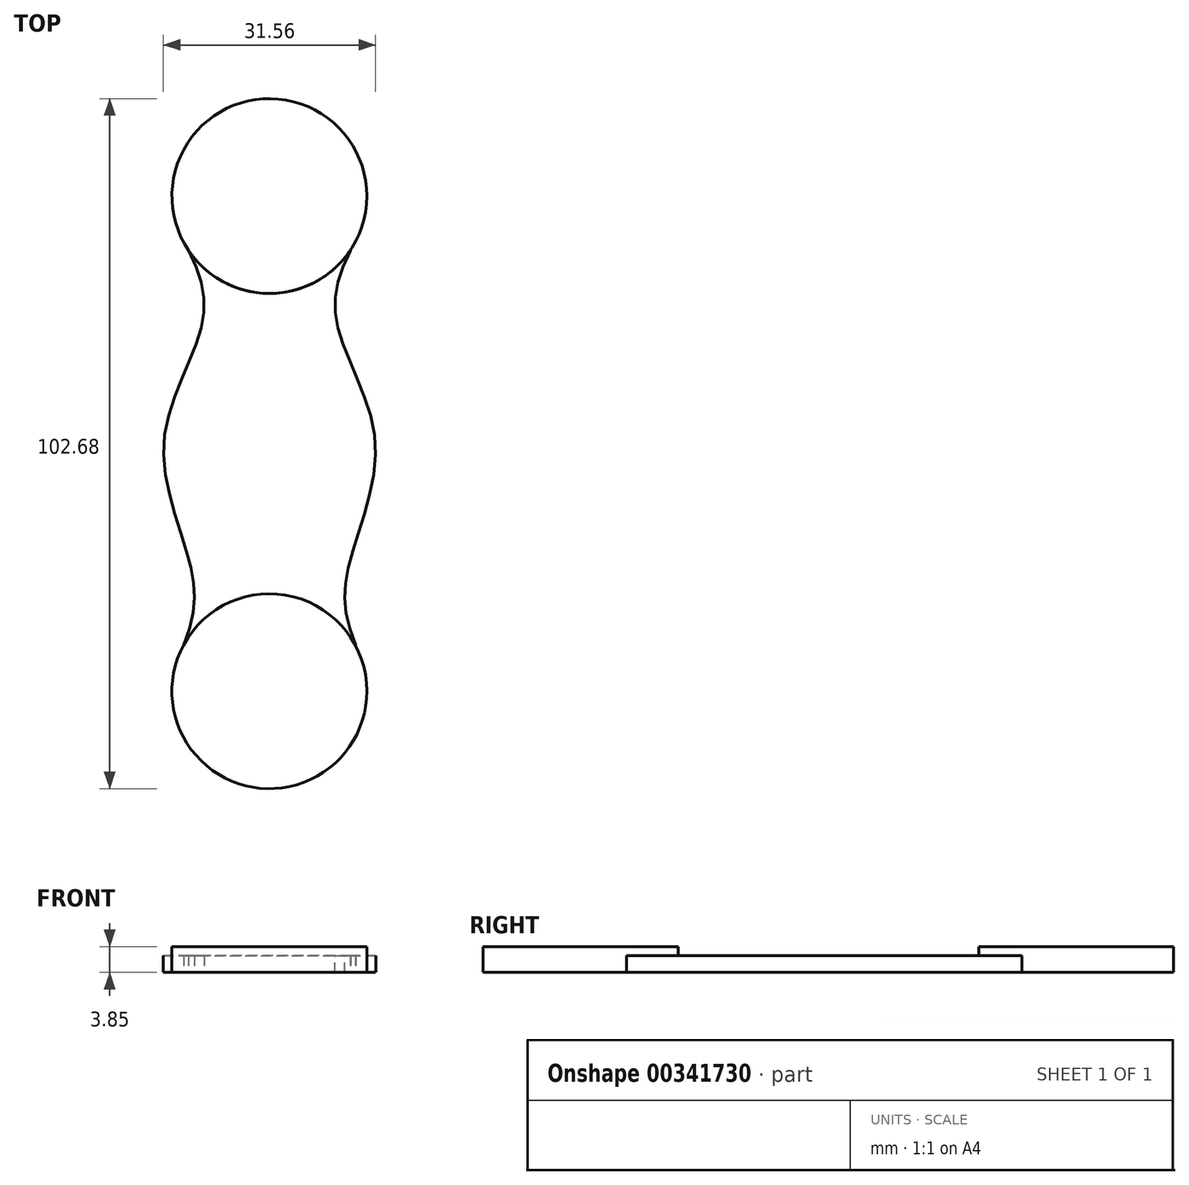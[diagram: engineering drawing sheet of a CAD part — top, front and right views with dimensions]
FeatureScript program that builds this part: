
annotation { "Feature Type Name" : "Feature", "Feature Type Description" : "" }
export const myFeature = defineFeature(function(context is Context, id is Id, definition is map)
    precondition{}
    {
        {
            var Q0;
            Q0=qCreatedBy(makeId("Top.planeOp"),FACE);
            var sketch = newSketch(context, id + "F0", { "sketchPlane" : qUnion([Q0])});
            skCircle(sketch, "E0", {"center": v(-0.03, 36.84) * mm, "radius": 14.5 * mm});
            skPoint(sketch, "E0.first.point", {"position": v(-14.52, 37.09) * mm});
            skPoint(sketch, "E0.second.point", {"position": v(14.47, 36.66) * mm});
            skPoint(sketch, "E0.third.point", {"position": v(0, 22.34) * mm});
            skSolve(sketch);
        }
        {
            var Q0;
            Q0=makeQuery(id+"F0.imprint","IMPRINT",FACE,{"disambiguationData":[TD([[makeQuery(id+"F0.imprint","IMPRINT",EDGE,{"derivedFrom":sQuery(id+"F0.wireOp",EDGE,"E0")}),1.0]])]});
            extrude(context, id + "F1", {"entities" : qUnion([Q0]), "depth" : 2.5 * mm});
        }
        {
            var Q0;
            Q0=makeQuery(id+"F1.opExtrude","SWEPT_BODY",BODY,{"disambiguationData":[OSD([sQuery(id+"F0.wireOp",EDGE,"E0")])]});
            var Q1;
            Q1=makeQuery(id+"F1.opExtrude","CAP_FACE",FACE,{"disambiguationData":[OSD([sQuery(id+"F0.wireOp",EDGE,"E0")])],"isStart":false});
            var Q2;
            Q2=qCreatedBy(makeId("Front.planeOp"),FACE);
            mirror(context, id + "F2", {"operationType" : NewBodyOperationType.ADD, "entities" : qUnion([Q0]), "faces" : qUnion([Q1]), "mirrorPlane" : qUnion([Q2])});
        }
        {
            var Q0;
            Q0=qCreatedBy(makeId("Top.planeOp"),FACE);
            var sketch = newSketch(context, id + "F3", { "sketchPlane" : qUnion([Q0])});
            skFitSpline(sketch, "E1", {"points": [v(-12.09, 28.75) * mm, v(-10.3, 16.8) * mm, v(-15.75, 0) * mm, v(-11.76, -18.16) * mm, v(-12.82, -30.03) * mm], "startDerivative": vector(31.75, -58.25) * mm, "endDerivative": vector(-25.02, -61.58) * mm});
            skFitSpline(sketch, "E2.MirrorCS", {"points": [v(12.09, 28.75) * mm, v(10.3, 16.8) * mm, v(15.75, 0) * mm, v(11.76, -18.16) * mm, v(12.82, -30.03) * mm], "startDerivative": vector(-31.75, -58.25) * mm, "endDerivative": vector(25.02, -61.58) * mm});
            skLineSegment(sketch, "E3", {"start": v(-12.09, 28.75) * mm, "end": v(12.09, 28.75) * mm});
            skLineSegment(sketch, "E4", {"start": v(-12.82, -30.03) * mm, "end": v(12.82, -30.03) * mm});
            skSolve(sketch);
        }
        {
            var Q0;
            Q0=makeQuery(id+"F3.imprint","IMPRINT",FACE,{"disambiguationData":[TD([[makeQuery(id+"F3.imprint","IMPRINT",EDGE,{"derivedFrom":sQuery(id+"F3.wireOp",EDGE,"E1")}),1.0]])]});
            extrude(context, id + "F4", {"entities" : qUnion([Q0]), "operationType" : NewBodyOperationType.ADD, "depth" : 2.5 * mm});
        }
        {
            var Q0;
            {var subQ0=makeQuery(id+"F1.opExtrude","CAP_FACE",FACE,{"disambiguationData":[OSD([sQuery(id+"F0.wireOp",EDGE,"E0")])],"isStart":false});Q0=makeQuery(id+"F4.boolean.opBoolean","MERGE",FACE,{"derivedFrom":[subQ0,makeQuery(id+"F2.opPattern","COPY",FACE,{"derivedFrom":subQ0,"instanceName":"1"}),makeQuery(id+"F4.opExtrude","CAP_FACE",FACE,{"disambiguationData":[OSD([sQuery(id+"F3.wireOp",EDGE,"E1"),sQuery(id+"F3.wireOp",EDGE,"E2.MirrorCS"),sQuery(id+"F3.wireOp",EDGE,"E3"),sQuery(id+"F3.wireOp",EDGE,"E4")])],"isStart":false})]});}
            var sketch = newSketch(context, id + "F5", { "sketchPlane" : qUnion([Q0])});
            skCircle(sketch, "E5", {"center": v(-0.03, 36.84) * mm, "radius": 14.5 * mm});
            skCircle(sketch, "E6", {"center": v(-0.03, -36.84) * mm, "radius": 14.5 * mm});
            skSolve(sketch);
        }
        {
            var Q0;
            Q0 = qSketchRegion(id + "F5", true);
            extrude(context, id + "F6", {"entities" : qUnion([Q0]), "operationType" : NewBodyOperationType.ADD, "depth" : 1.35 * mm});
        }
    });
